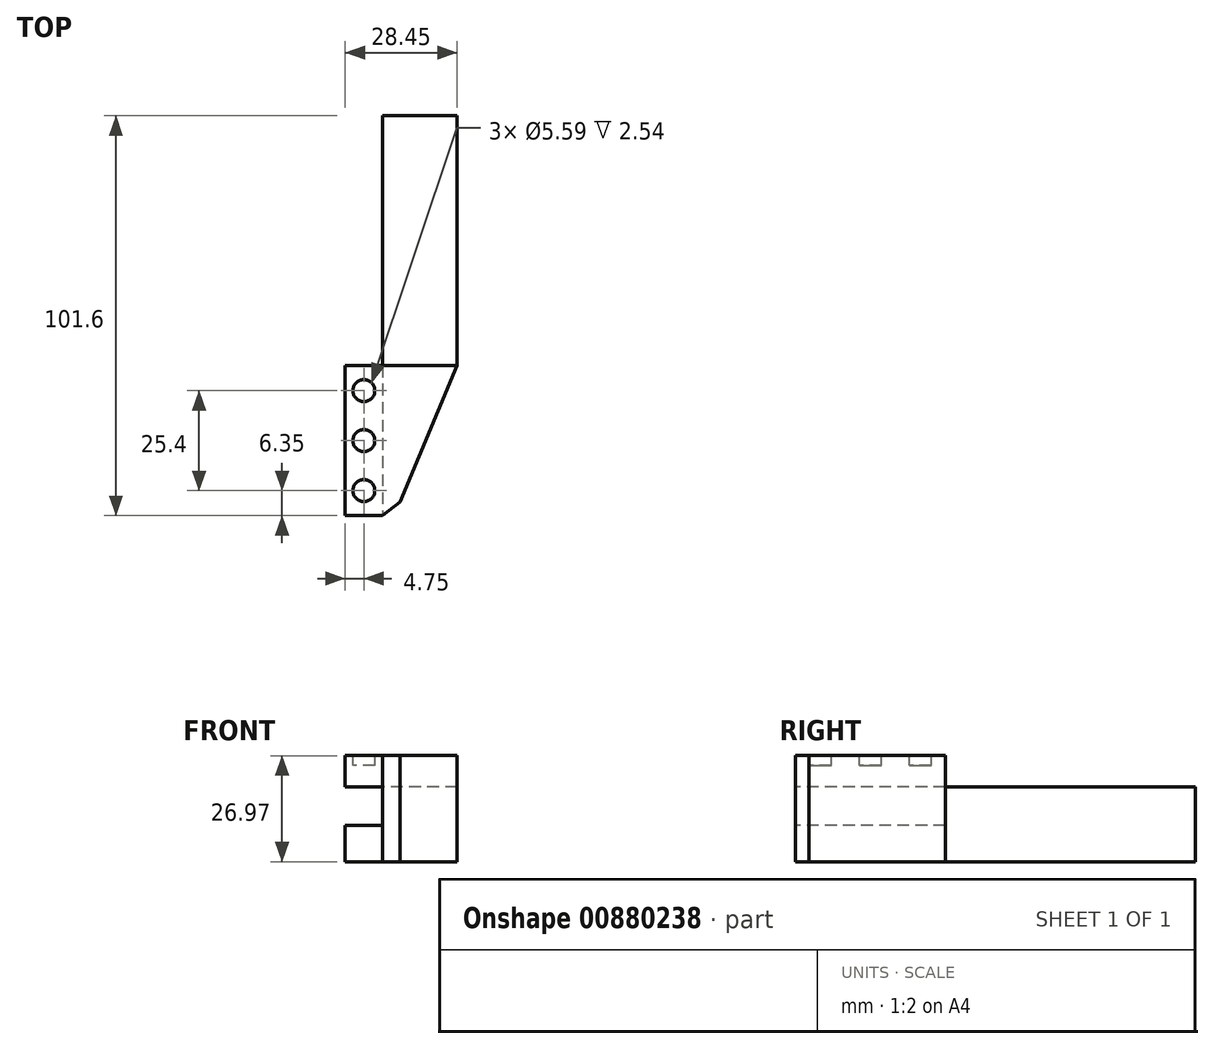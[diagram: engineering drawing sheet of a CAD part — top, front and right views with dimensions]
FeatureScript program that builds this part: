
annotation { "Feature Type Name" : "Feature", "Feature Type Description" : "" }
export const myFeature = defineFeature(function(context is Context, id is Id, definition is map)
    precondition{}
    {
        {
            var Q0;
            Q0=qCreatedBy(makeId("Top.planeOp"),FACE);
            var sketch = newSketch(context, id + "F0", { "sketchPlane" : qUnion([Q0])});
            skLineSegment(sketch, "E0", {"start": v(0, 0) * mm, "end": v(9.53, 0) * mm});
            skLineSegment(sketch, "E1", {"start": v(9.52, 0) * mm, "end": v(13.95, 3.42) * mm});
            skLineSegment(sketch, "E2", {"start": v(0, 0) * mm, "end": v(0, 38.1) * mm});
            skLineSegment(sketch, "E3", {"start": v(28.45, 38.1) * mm, "end": v(13.95, 3.42) * mm});
            skLineSegment(sketch, "E4", {"start": v(28.45, 38.1) * mm, "end": v(0, 38.1) * mm});
            skSolve(sketch);
        }
        {
            var Q0;
            Q0=qSketchRegion(id+"F0",true);
            extrude(context, id + "F1", {"entities" : qUnion([Q0]), "depth" : 26.97 * mm});
        }
        {
            var Q0;
            Q0=makeQuery(id+"F1.opExtrude","SWEPT_FACE",FACE,{"disambiguationData":[OSD([sQuery(id+"F0.wireOp",EDGE,"E2")])]});
            var sketch = newSketch(context, id + "F2", { "sketchPlane" : qUnion([Q0])});
            skLineSegment(sketch, "E5.bottom", {"start": v(-38.1, 9.27) * mm, "end": v(0, 9.27) * mm});
            skLineSegment(sketch, "E5.top", {"start": v(-38.1, 19.05) * mm, "end": v(0, 19.05) * mm});
            skLineSegment(sketch, "E5.left", {"start": v(-38.1, 9.27) * mm, "end": v(-38.1, 19.05) * mm});
            skLineSegment(sketch, "E5.right", {"start": v(0, 9.27) * mm, "end": v(0, 19.05) * mm});
            skSolve(sketch);
        }
        {
            var Q0;
            Q0=qSketchRegion(id+"F2",true);
            extrude(context, id + "F3", {"entities" : qUnion([Q0]), "operationType" : NewBodyOperationType.REMOVE, "oppositeDirection" : true, "depth" : 9.52 * mm});
        }
        {
            var Q0;
            Q0=makeQuery(id+"F1.opExtrude","SWEPT_FACE",FACE,{"disambiguationData":[OSD([sQuery(id+"F0.wireOp",EDGE,"E4")])]});
            var sketch = newSketch(context, id + "F4", { "sketchPlane" : qUnion([Q0])});
            skLineSegment(sketch, "E6.bottom", {"start": v(-28.45, 0) * mm, "end": v(-9.53, 0) * mm});
            skLineSegment(sketch, "E6.top", {"start": v(-28.45, 19.05) * mm, "end": v(-9.53, 19.05) * mm});
            skLineSegment(sketch, "E6.left", {"start": v(-28.45, 0) * mm, "end": v(-28.45, 19.05) * mm});
            skLineSegment(sketch, "E6.right", {"start": v(-9.53, 0) * mm, "end": v(-9.53, 19.05) * mm});
            skSolve(sketch);
        }
        {
            var Q0;
            Q0=qSketchRegion(id+"F4",true);
            extrude(context, id + "F5", {"entities" : qUnion([Q0]), "operationType" : NewBodyOperationType.ADD, "depth" : 63.5 * mm});
        }
        {
            var Q0;
            Q0=makeQuery(id+"F1.opExtrude","CAP_FACE",FACE,{"disambiguationData":[OSD([sQuery(id+"F0.wireOp",EDGE,"E0"),sQuery(id+"F0.wireOp",EDGE,"E1"),sQuery(id+"F0.wireOp",EDGE,"E2"),sQuery(id+"F0.wireOp",EDGE,"E3"),sQuery(id+"F0.wireOp",EDGE,"E4")])],"isStart":false});
            var sketch = newSketch(context, id + "F6", { "sketchPlane" : qUnion([Q0])});
            skCircle(sketch, "E7", {"center": v(4.75, 31.75) * mm, "radius": 2.8 * mm});
            skCircle(sketch, "E8", {"center": v(4.75, 19.05) * mm, "radius": 2.8 * mm});
            skCircle(sketch, "E9", {"center": v(4.75, 6.35) * mm, "radius": 2.8 * mm});
            skSolve(sketch);
        }
        {
            var Q0;
            Q0=qSketchRegion(id+"F6",true);
            extrude(context, id + "F7", {"entities" : qUnion([Q0]), "operationType" : NewBodyOperationType.REMOVE, "oppositeDirection" : true, "depth" : 2.54 * mm});
        }
    });
